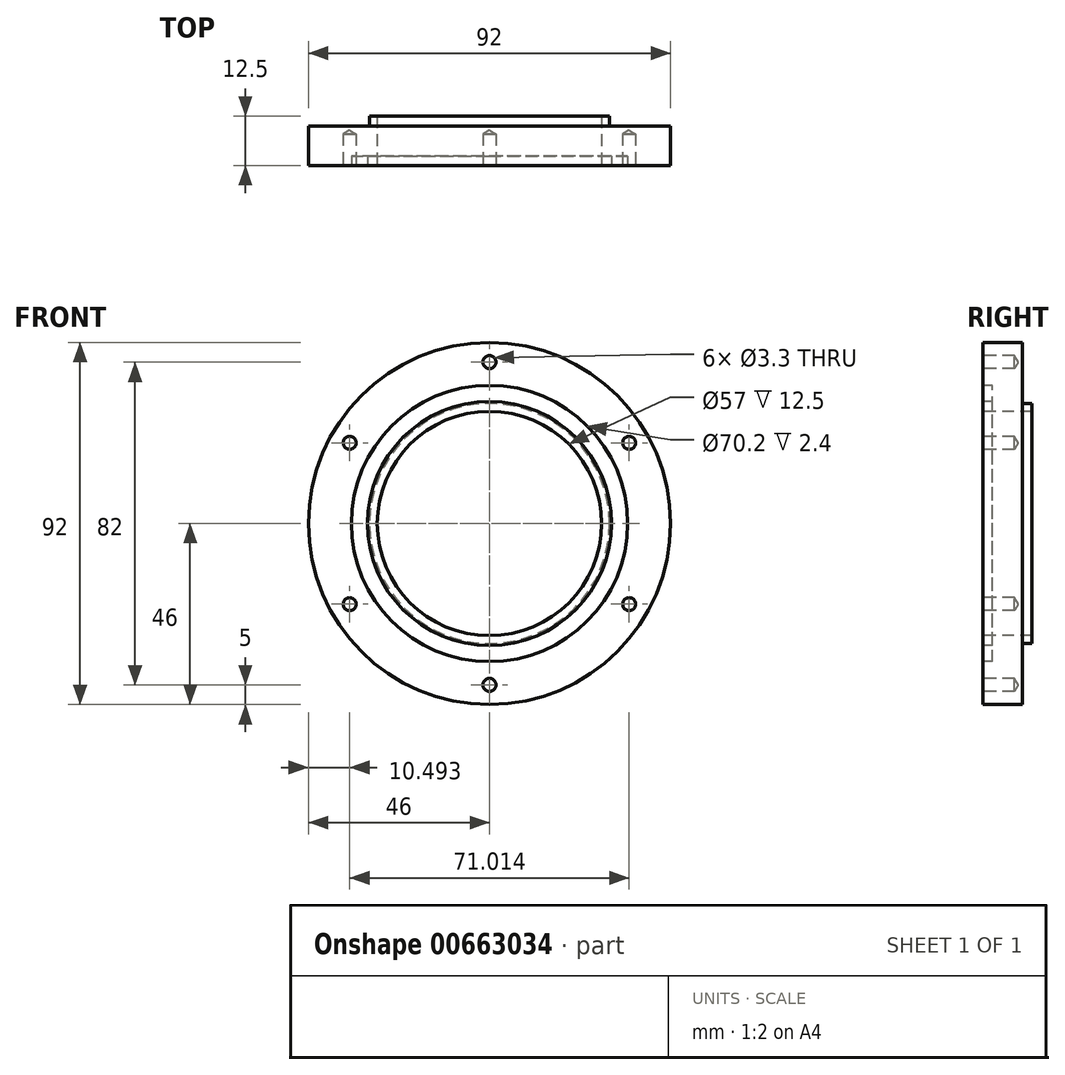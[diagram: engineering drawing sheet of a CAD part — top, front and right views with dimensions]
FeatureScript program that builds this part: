
annotation { "Feature Type Name" : "Feature", "Feature Type Description" : "" }
export const myFeature = defineFeature(function(context is Context, id is Id, definition is map)
    precondition{}
    {
        {
            var Q0;
            Q0=qCreatedBy(makeId("Front.planeOp"),FACE);
            var sketch = newSketch(context, id + "F0", { "sketchPlane" : qUnion([Q0])});
            skCircle(sketch, "E0", {"center": v(0, 0) * mm, "radius": 46 * mm});
            skCircle(sketch, "E1", {"center": v(0, 0) * mm, "radius": 28.5 * mm});
            skSolve(sketch);
        }
        {
            var Q0;
            Q0=makeQuery(id+"F0.imprint","IMPRINT",FACE,{"disambiguationData":[TD([[makeQuery(id+"F0.imprint","IMPRINT",EDGE,{"derivedFrom":sQuery(id+"F0.wireOp",EDGE,"E0")}),1.0]])]});
            extrude(context, id + "F1", {"entities" : qUnion([Q0]), "oppositeDirection" : true, "depth" : 10 * mm, "offsetDistance" : 25 * mm});
        }
        {
            var Q0;
            Q0=makeQuery(id+"F1.opExtrude","CAP_FACE",FACE,{"disambiguationData":[OSD([sQuery(id+"F0.wireOp",EDGE,"E0"),sQuery(id+"F0.wireOp",EDGE,"E1")])],"isStart":true});
            var sketch = newSketch(context, id + "F2", { "sketchPlane" : qUnion([Q0])});
            skCircle(sketch, "E2", {"center": v(0, 0) * mm, "radius": 35.1 * mm});
            skCircle(sketch, "E3", {"center": v(0, 0) * mm, "radius": 31 * mm});
            skSolve(sketch);
        }
        {
            var Q0;
            Q0=makeQuery(id+"F2.imprint","IMPRINT",FACE,{"disambiguationData":[TD([[makeQuery(id+"F2.imprint","IMPRINT",EDGE,{"derivedFrom":sQuery(id+"F2.wireOp",EDGE,"E2")}),1.0]])]});
            extrude(context, id + "F3", {"entities" : qUnion([Q0]), "operationType" : NewBodyOperationType.REMOVE, "oppositeDirection" : true, "depth" : 2.4 * mm, "offsetDistance" : 25 * mm});
        }
        {
            var Q0;
            {var subQ0=sQuery(id+"F0.wireOp",EDGE,"E0");Q0=makeQuery(id+"F3.boolean.opBoolean","SPLIT",FACE,{"disambiguationData":[TD([makeQuery(id+"F1.opExtrude","SWEPT_FACE",FACE,{"disambiguationData":[OSD([subQ0])]})])],"derivedFrom":makeQuery(id+"F1.opExtrude","CAP_FACE",FACE,{"disambiguationData":[OSD([subQ0,sQuery(id+"F0.wireOp",EDGE,"E1")])],"isStart":true})});}
            var sketch = newSketch(context, id + "F4", { "sketchPlane" : qUnion([Q0])});
            skPoint(sketch, "E4", {"position": v(0, 41) * mm});
            skPoint(sketch, "E5.1.0", {"position": v(-35.5, 20.5) * mm});
            skPoint(sketch, "E5.2.0", {"position": v(-35.5, -20.5) * mm});
            skPoint(sketch, "E5.3.0", {"position": v(0, -41) * mm});
            skPoint(sketch, "E5.4.0", {"position": v(35.5, -20.5) * mm});
            skPoint(sketch, "E5.5.0", {"position": v(35.5, 20.5) * mm});
            skPoint(sketch, "E5.center", {"position": v(0, 0) * mm});
            skSolve(sketch);
        }
        {
            var Q0;
            Q0=sQuery(id+"F4.wireOp",VERTEX,"E4");
            var Q1;
            Q1=sQuery(id+"F4.wireOp",VERTEX,"E5.5.0");
            var Q2;
            Q2=sQuery(id+"F4.wireOp",VERTEX,"E5.4.0");
            var Q3;
            Q3=sQuery(id+"F4.wireOp",VERTEX,"E5.3.0");
            var Q4;
            Q4=sQuery(id+"F4.wireOp",VERTEX,"E5.2.0");
            var Q5;
            Q5=sQuery(id+"F4.wireOp",VERTEX,"E5.1.0");
            var Q6;
            Q6=makeQuery(id+"F1.opExtrude","SWEPT_BODY",BODY,{"disambiguationData":[OSD([sQuery(id+"F0.wireOp",EDGE,"E0"),sQuery(id+"F0.wireOp",EDGE,"E1")])]});
            hole(context, id + "F5", {"style" : HoleStyle.SIMPLE, "endStyle" : HoleEndStyle.BLIND, "standardTappedOrClearance" : lookupTablePath({ "standard" : "ISO", "engagement" : "75%", "pitch" : "0.7 mm", "size" : "M4", "type" : "Tapped" }), "standardBlindInLast" : lookupTablePath({ "standard" : "ISO", "engagement" : "75%", "pitch" : "0.7 mm", "size" : "M4", "type" : "Tapped" }), "holeDiameter" : 3.3 * mm, "majorDiameter" : 4 * mm, "showTappedDepth" : true, "holeDepth" : 8 * mm, "isTappedThrough" : true, "tappedDepth" : 5.9 * mm, "tapClearance" : 3, "locations" : qUnion([Q0, Q1, Q2, Q3, Q4, Q5]), "scope" : qUnion([Q6])});
        }
        {
            var Q0;
            Q0=makeQuery(id+"F1.opExtrude","CAP_FACE",FACE,{"disambiguationData":[OSD([sQuery(id+"F0.wireOp",EDGE,"E0"),sQuery(id+"F0.wireOp",EDGE,"E1")])],"isStart":false});
            var sketch = newSketch(context, id + "F6", { "sketchPlane" : qUnion([Q0])});
            skCircle(sketch, "E6", {"center": v(0, 0) * mm, "radius": 28.5 * mm});
            skCircle(sketch, "E7", {"center": v(0, 0) * mm, "radius": 30.5 * mm});
            skSolve(sketch);
        }
        {
            var Q0;
            Q0=makeQuery(id+"F6.imprint","IMPRINT",FACE,{"disambiguationData":[TD([[makeQuery(id+"F6.imprint","IMPRINT",EDGE,{"derivedFrom":sQuery(id+"F6.wireOp",EDGE,"E6")}),1.0]])]});
            extrude(context, id + "F7", {"entities" : qUnion([Q0]), "operationType" : NewBodyOperationType.ADD, "depth" : 2.5 * mm, "offsetDistance" : 25 * mm});
        }
    });
